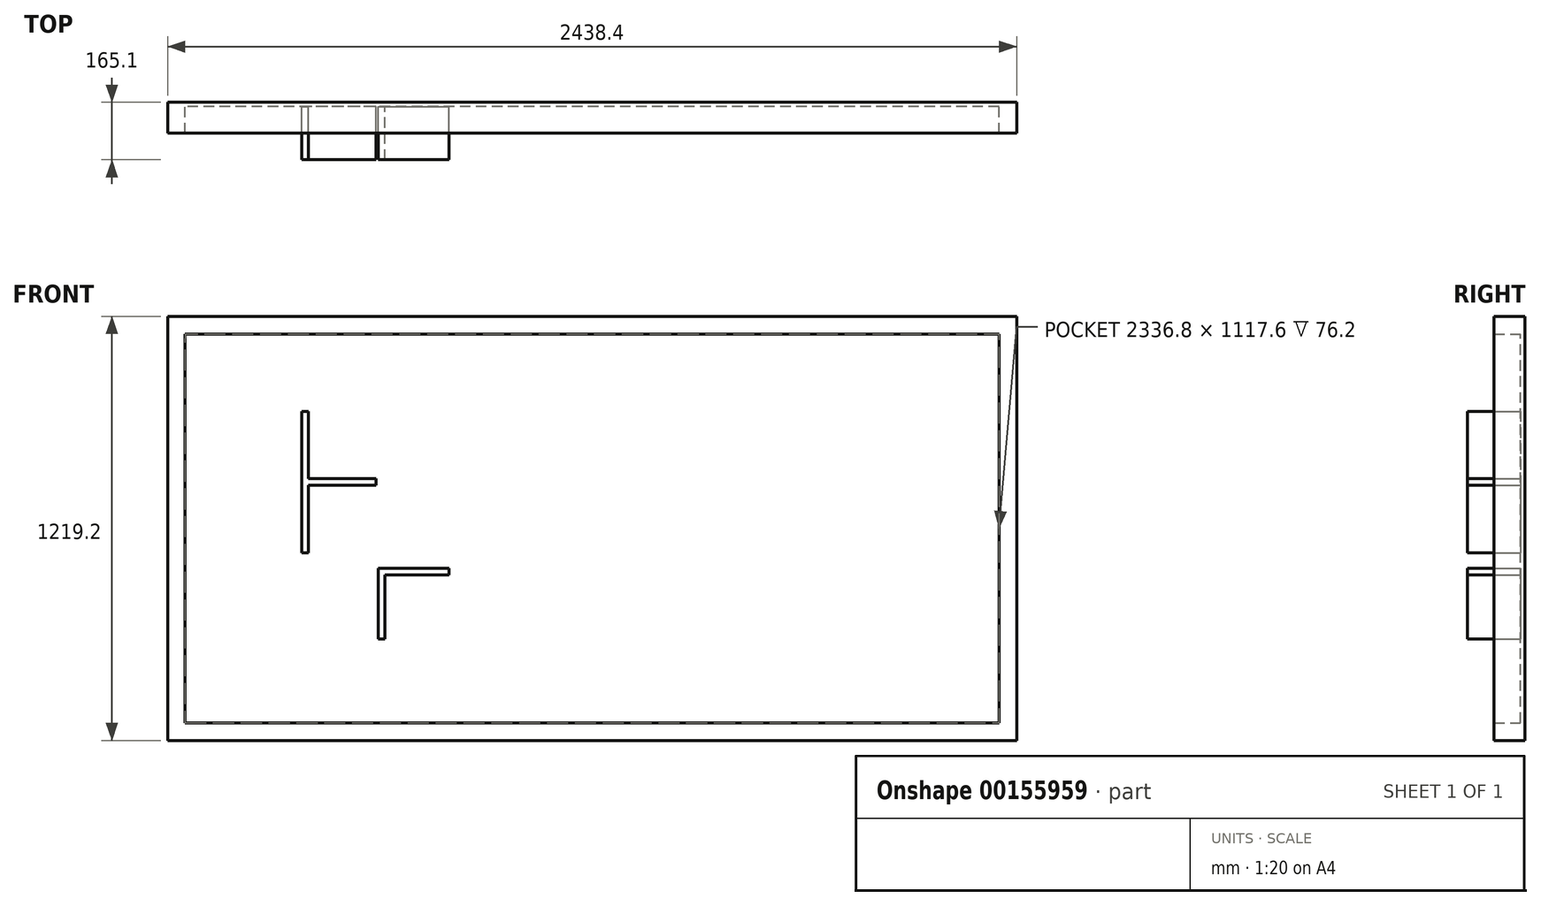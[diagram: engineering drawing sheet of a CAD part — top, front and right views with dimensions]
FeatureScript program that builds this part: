
annotation { "Feature Type Name" : "Feature", "Feature Type Description" : "" }
export const myFeature = defineFeature(function(context is Context, id is Id, definition is map)
    precondition{}
    {
        {
            var Q0;
            Q0=qCreatedBy(makeId("Front.planeOp"),FACE);
            var sketch = newSketch(context, id + "F0", { "sketchPlane" : qUnion([Q0])});
            skLineSegment(sketch, "E0.bottom", {"start": v(-1219.2, 609.6) * mm, "end": v(1219.2, 609.6) * mm});
            skLineSegment(sketch, "E0.top", {"start": v(-1219.2, -609.6) * mm, "end": v(1219.2, -609.6) * mm});
            skLineSegment(sketch, "E0.left", {"start": v(-1219.2, 609.6) * mm, "end": v(-1219.2, -609.6) * mm});
            skLineSegment(sketch, "E0.right", {"start": v(1219.2, 609.6) * mm, "end": v(1219.2, -609.6) * mm});
            skLineSegment(sketch, "E1.0", {"start": v(-1168.4, 558.8) * mm, "end": v(1168.4, 558.8) * mm});
            skLineSegment(sketch, "E1.1", {"start": v(-1168.4, 558.8) * mm, "end": v(-1168.4, -558.8) * mm});
            skLineSegment(sketch, "E1.2", {"start": v(-1168.4, -558.8) * mm, "end": v(1168.4, -558.8) * mm});
            skLineSegment(sketch, "E1.3", {"start": v(1168.4, 558.8) * mm, "end": v(1168.4, -558.8) * mm});
            skSolve(sketch);
        }
        {
            var Q0;
            Q0=makeQuery(id+"F0.imprint","IMPRINT",FACE,{"disambiguationData":[TD([[makeQuery(id+"F0.imprint","IMPRINT",EDGE,{"derivedFrom":sQuery(id+"F0.wireOp",EDGE,"E1.0")}),-1.0]])]});
            var Q1;
            Q1=makeQuery(id+"F0.imprint","IMPRINT",FACE,{"disambiguationData":[TD([[makeQuery(id+"F0.imprint","IMPRINT",EDGE,{"derivedFrom":sQuery(id+"F0.wireOp",EDGE,"E0.bottom")}),-1.0]])]});
            extrude(context, id + "F1", {"entities" : qUnion([Q0, Q1]), "depth" : 12.7 * mm});
        }
        {
            var Q0;
            Q0=makeQuery(id+"F0.imprint","IMPRINT",FACE,{"disambiguationData":[TD([[makeQuery(id+"F0.imprint","IMPRINT",EDGE,{"derivedFrom":sQuery(id+"F0.wireOp",EDGE,"E0.bottom")}),-1.0]])]});
            extrude(context, id + "F2", {"entities" : qUnion([Q0]), "operationType" : NewBodyOperationType.ADD, "depth" : 88.9 * mm});
        }
        {
            var Q0;
            Q0=makeQuery(id+"F1.opExtrude","CAP_FACE",FACE,{"disambiguationData":[OSD([sQuery(id+"F0.wireOp",EDGE,"E0.bottom"),sQuery(id+"F0.wireOp",EDGE,"E0.top"),sQuery(id+"F0.wireOp",EDGE,"E0.left"),sQuery(id+"F0.wireOp",EDGE,"E0.right")])],"isStart":false});
            var sketch = newSketch(context, id + "F3", { "sketchPlane" : qUnion([Q0])});
            skLineSegment(sketch, "E2.bottom", {"start": v(-833.32, 336.38) * mm, "end": v(-814.27, 336.38) * mm});
            skLineSegment(sketch, "E2.top", {"start": v(-833.32, -70.02) * mm, "end": v(-814.27, -70.02) * mm});
            skLineSegment(sketch, "E2.left", {"start": v(-833.32, 336.38) * mm, "end": v(-833.32, 142.7) * mm});
            skLineSegment(sketch, "E2.right", {"start": v(-814.27, 336.38) * mm, "end": v(-814.27, 142.7) * mm});
            skLineSegment(sketch, "E3.bottom", {"start": v(-620.6, 142.7) * mm, "end": v(-814.27, 142.7) * mm});
            skLineSegment(sketch, "E3.top", {"start": v(-620.6, 123.65) * mm, "end": v(-814.27, 123.65) * mm});
            skLineSegment(sketch, "E3.left", {"start": v(-620.6, 142.7) * mm, "end": v(-620.6, 123.65) * mm});
            skLineSegment(sketch, "E4.trimOffspring", {"start": v(-814.27, 123.65) * mm, "end": v(-814.27, -70.02) * mm});
            skLineSegment(sketch, "E5.trimOffspring", {"start": v(-833.32, 123.65) * mm, "end": v(-833.32, -70.02) * mm});
            skLineSegment(sketch, "E6", {"start": v(-833.32, 142.7) * mm, "end": v(-833.32, 123.65) * mm});
            skSolve(sketch);
        }
        {
            var Q0;
            Q0=makeQuery(id+"F3.imprint","IMPRINT",FACE,{"disambiguationData":[TD([[makeQuery(id+"F3.imprint","IMPRINT",EDGE,{"derivedFrom":sQuery(id+"F3.wireOp",EDGE,"E2.bottom")}),-1.0]])]});
            extrude(context, id + "F4", {"entities" : qUnion([Q0]), "depth" : 152.4 * mm});
        }
        {
            var Q0;
            Q0=makeQuery(id+"F1.opExtrude","CAP_FACE",FACE,{"disambiguationData":[OSD([sQuery(id+"F0.wireOp",EDGE,"E0.bottom"),sQuery(id+"F0.wireOp",EDGE,"E0.top"),sQuery(id+"F0.wireOp",EDGE,"E0.left"),sQuery(id+"F0.wireOp",EDGE,"E0.right")])],"isStart":false});
            var sketch = newSketch(context, id + "F5", { "sketchPlane" : qUnion([Q0])});
            skLineSegment(sketch, "E7.bottom", {"start": v(-594.93, -133.87) * mm, "end": v(-410.78, -133.87) * mm});
            skLineSegment(sketch, "E7.top", {"start": v(-613.98, -114.82) * mm, "end": v(-410.78, -114.82) * mm});
            skLineSegment(sketch, "E7.left", {"start": v(-613.98, -114.82) * mm, "end": v(-613.98, -133.87) * mm});
            skLineSegment(sketch, "E7.right", {"start": v(-410.78, -114.82) * mm, "end": v(-410.78, -133.87) * mm});
            skLineSegment(sketch, "E8.bottom", {"start": v(-613.98, -114.82) * mm, "end": v(-594.93, -114.82) * mm});
            skLineSegment(sketch, "E8.top", {"start": v(-613.98, -318.02) * mm, "end": v(-594.93, -318.02) * mm});
            skLineSegment(sketch, "E8.left", {"start": v(-613.98, -114.82) * mm, "end": v(-613.98, -318.02) * mm});
            skLineSegment(sketch, "E8.right", {"start": v(-594.93, -133.87) * mm, "end": v(-594.93, -318.02) * mm});
            skSolve(sketch);
        }
        {
            var Q0;
            Q0=makeQuery(id+"F5.imprint","IMPRINT",FACE,{"disambiguationData":[TD([[makeQuery(id+"F5.imprint","IMPRINT",EDGE,{"derivedFrom":sQuery(id+"F5.wireOp",EDGE,"E7.bottom")}),1.0]])]});
            extrude(context, id + "F6", {"entities" : qUnion([Q0]), "depth" : 152.4 * mm});
        }
    });
